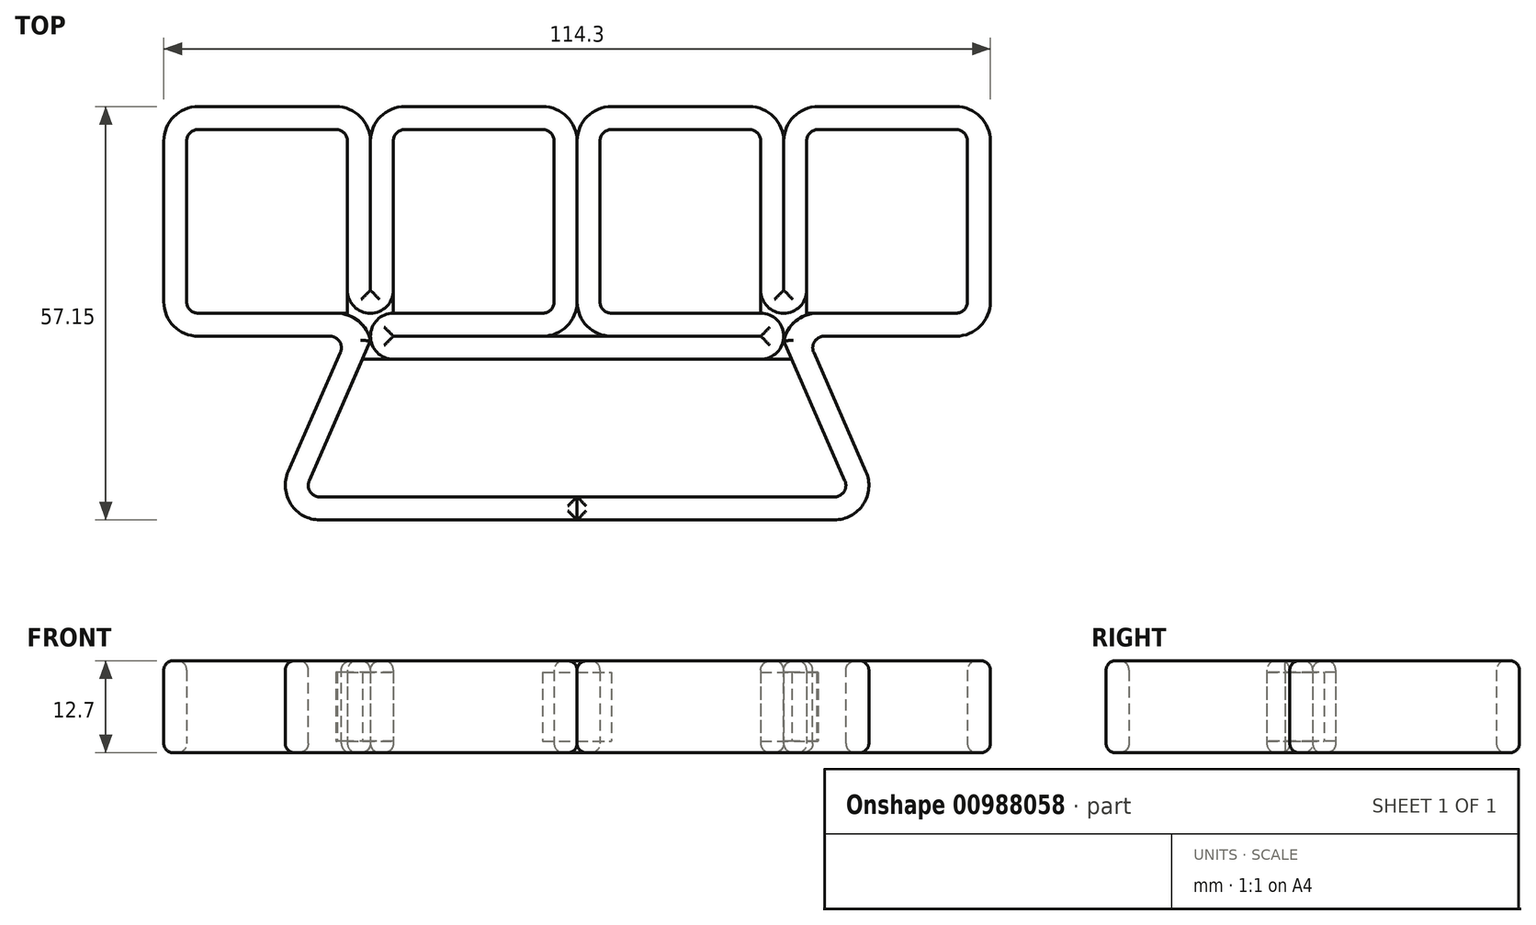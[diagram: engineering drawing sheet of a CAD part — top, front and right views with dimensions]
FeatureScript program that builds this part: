
annotation { "Feature Type Name" : "Feature", "Feature Type Description" : "" }
export const myFeature = defineFeature(function(context is Context, id is Id, definition is map)
    precondition{}
    {
        {
            var Q0;
            Q0=qCreatedBy(makeId("Top.planeOp"),FACE);
            var sketch = newSketch(context, id + "F0", { "sketchPlane" : qUnion([Q0])});
            skLineSegment(sketch, "E0.bottom", {"start": v(3.18, 3.17) * mm, "end": v(25.4, 3.18) * mm});
            skLineSegment(sketch, "E0.top", {"start": v(3.17, 28.58) * mm, "end": v(25.4, 28.58) * mm});
            skLineSegment(sketch, "E0.left", {"start": v(3.18, 3.18) * mm, "end": v(3.17, 28.57) * mm});
            skLineSegment(sketch, "E0.right", {"start": v(25.4, 3.18) * mm, "end": v(25.4, 28.58) * mm});
            skLineSegment(sketch, "E1.bottom", {"start": v(-3.17, 3.17) * mm, "end": v(-25.4, 3.17) * mm});
            skLineSegment(sketch, "E1.top", {"start": v(-3.18, 28.58) * mm, "end": v(-25.4, 28.57) * mm});
            skLineSegment(sketch, "E1.left", {"start": v(-3.17, 3.18) * mm, "end": v(-3.18, 28.57) * mm});
            skLineSegment(sketch, "E1.right", {"start": v(-25.4, 3.17) * mm, "end": v(-25.4, 28.57) * mm});
            skLineSegment(sketch, "E2", {"start": v(-25.4, 0) * mm, "end": v(25.4, 0) * mm});
            skLineSegment(sketch, "E3", {"start": v(-25.4, 3.17) * mm, "end": v(-28.58, 3.17) * mm});
            skLineSegment(sketch, "E4", {"start": v(-28.58, 3.18) * mm, "end": v(-28.58, -3.18) * mm});
            skLineSegment(sketch, "E5", {"start": v(-28.58, -3.18) * mm, "end": v(28.58, -3.17) * mm});
            skLineSegment(sketch, "E6", {"start": v(28.58, -3.18) * mm, "end": v(28.58, 3.18) * mm});
            skLineSegment(sketch, "E7", {"start": v(28.58, 3.18) * mm, "end": v(25.4, 3.18) * mm});
            skLineSegment(sketch, "E8", {"start": v(0, 0) * mm, "end": v(0, 31.75) * mm});
            skLineSegment(sketch, "E9", {"start": v(0, 31.75) * mm, "end": v(28.58, 31.75) * mm});
            skLineSegment(sketch, "E10", {"start": v(28.57, 31.75) * mm, "end": v(28.57, 6.35) * mm});
            skLineSegment(sketch, "E11", {"start": v(28.58, 31.75) * mm, "end": v(57.15, 31.75) * mm});
            skLineSegment(sketch, "E12", {"start": v(57.15, 31.75) * mm, "end": v(57.15, 0) * mm});
            skLineSegment(sketch, "E13.bottom", {"start": v(31.75, 3.18) * mm, "end": v(53.98, 3.18) * mm});
            skLineSegment(sketch, "E13.top", {"start": v(31.75, 28.58) * mm, "end": v(53.98, 28.58) * mm});
            skLineSegment(sketch, "E13.left", {"start": v(31.75, 3.18) * mm, "end": v(31.75, 28.58) * mm});
            skLineSegment(sketch, "E13.right", {"start": v(53.98, 3.18) * mm, "end": v(53.98, 28.58) * mm});
            skLineSegment(sketch, "E14", {"start": v(31.75, 3.18) * mm, "end": v(28.58, 3.18) * mm});
            skLineSegment(sketch, "E15", {"start": v(57.15, 0) * mm, "end": v(31.75, 0) * mm});
            skLineSegment(sketch, "E16", {"start": v(31.75, 0) * mm, "end": v(42.86, -25.4) * mm});
            skPoint(sketch, "E16.endSnap0", {"position": v(42.86, 3.18) * mm});
            skLineSegment(sketch, "E17", {"start": v(42.86, -25.4) * mm, "end": v(0, -25.4) * mm});
            skLineSegment(sketch, "E18", {"start": v(0, -22.23) * mm, "end": v(38, -22.22) * mm});
            skLineSegment(sketch, "E19", {"start": v(38, -22.23) * mm, "end": v(28.58, -0.66) * mm});
            skLineSegment(sketch, "E20.MirrorCS", {"start": v(0, 31.75) * mm, "end": v(-28.58, 31.75) * mm});
            skLineSegment(sketch, "E21.MirrorCS", {"start": v(-31.75, 3.18) * mm, "end": v(-31.75, 28.58) * mm});
            skLineSegment(sketch, "E22.MirrorCS", {"start": v(-28.58, 31.75) * mm, "end": v(-28.58, 6.35) * mm});
            skLineSegment(sketch, "E23.MirrorCS", {"start": v(-28.58, 31.75) * mm, "end": v(-57.15, 31.75) * mm});
            skLineSegment(sketch, "E24.MirrorCS", {"start": v(-31.75, 28.58) * mm, "end": v(-53.98, 28.58) * mm});
            skLineSegment(sketch, "E25.MirrorCS", {"start": v(-31.75, 3.18) * mm, "end": v(-53.98, 3.18) * mm});
            skLineSegment(sketch, "E26.MirrorCS", {"start": v(-57.15, 31.75) * mm, "end": v(-57.15, 0) * mm});
            skLineSegment(sketch, "E27.MirrorCS", {"start": v(-53.98, 3.18) * mm, "end": v(-53.98, 28.58) * mm});
            skLineSegment(sketch, "E28.MirrorCS", {"start": v(-57.15, 0) * mm, "end": v(-31.75, 0) * mm});
            skLineSegment(sketch, "E29.MirrorCS", {"start": v(-31.75, 0) * mm, "end": v(-42.86, -25.4) * mm});
            skLineSegment(sketch, "E30.MirrorCS", {"start": v(-38, -22.23) * mm, "end": v(-28.58, -0.66) * mm});
            skLineSegment(sketch, "E31.MirrorCS", {"start": v(0, -22.23) * mm, "end": v(-38, -22.23) * mm});
            skLineSegment(sketch, "E32.MirrorCS", {"start": v(-42.86, -25.4) * mm, "end": v(0, -25.4) * mm});
            skLineSegment(sketch, "E33", {"start": v(-31.75, 3.17) * mm, "end": v(-28.58, 3.17) * mm});
            skLineSegment(sketch, "E34", {"start": v(0, -22.23) * mm, "end": v(0, -25.4) * mm});
            skLineSegment(sketch, "E35.bottom", {"start": v(-28.57, 6.35) * mm, "end": v(-28.58, 6.35) * mm});
            skLineSegment(sketch, "E35.top", {"start": v(-28.57, 31.75) * mm, "end": v(-28.58, 31.75) * mm});
            skLineSegment(sketch, "E35.left", {"start": v(-28.57, 6.35) * mm, "end": v(-28.57, 31.75) * mm});
            skLineSegment(sketch, "E35.right", {"start": v(-28.58, 6.35) * mm, "end": v(-28.58, 31.75) * mm});
            skPoint(sketch, "E35.middle", {"position": v(-28.58, 19.05) * mm});
            skLineSegment(sketch, "E36.bottom", {"start": v(-31.75, 3.17) * mm, "end": v(-25.4, 3.17) * mm});
            skLineSegment(sketch, "E36.top", {"start": v(-31.75, 3.18) * mm, "end": v(-25.4, 3.18) * mm});
            skLineSegment(sketch, "E36.left", {"start": v(-31.75, 3.18) * mm, "end": v(-31.75, 3.18) * mm});
            skLineSegment(sketch, "E36.right", {"start": v(-25.4, 3.18) * mm, "end": v(-25.4, 3.18) * mm});
            skLineSegment(sketch, "E37.bottom", {"start": v(0, 0) * mm, "end": v(0, 0) * mm});
            skLineSegment(sketch, "E37.top", {"start": v(0, 31.75) * mm, "end": v(0, 31.75) * mm});
            skPoint(sketch, "E37.middle", {"position": v(0, 15.87) * mm});
            skLineSegment(sketch, "E38.left", {"start": v(-25.4, 0) * mm, "end": v(-25.4, 0) * mm});
            skLineSegment(sketch, "E38.right", {"start": v(25.4, 0) * mm, "end": v(25.4, 0) * mm});
            skLineSegment(sketch, "E39.bottom", {"start": v(28.58, 6.35) * mm, "end": v(28.57, 6.35) * mm});
            skLineSegment(sketch, "E39.top", {"start": v(28.58, 31.75) * mm, "end": v(28.57, 31.75) * mm});
            skLineSegment(sketch, "E39.left", {"start": v(28.58, 6.35) * mm, "end": v(28.58, 31.75) * mm});
            skLineSegment(sketch, "E39.right", {"start": v(28.57, 6.35) * mm, "end": v(28.57, 31.75) * mm});
            skPoint(sketch, "E39.middle", {"position": v(28.58, 19.05) * mm});
            skLineSegment(sketch, "E40.bottom", {"start": v(25.4, 3.18) * mm, "end": v(31.75, 3.18) * mm});
            skLineSegment(sketch, "E40.top", {"start": v(25.4, 3.18) * mm, "end": v(31.75, 3.18) * mm});
            skLineSegment(sketch, "E40.left", {"start": v(25.4, 3.18) * mm, "end": v(25.4, 3.18) * mm});
            skLineSegment(sketch, "E40.right", {"start": v(31.75, 3.18) * mm, "end": v(31.75, 3.18) * mm});
            skLineSegment(sketch, "E41.bottom", {"start": v(28.58, 3.18) * mm, "end": v(28.57, 3.18) * mm});
            skLineSegment(sketch, "E41.top", {"start": v(28.58, -3.17) * mm, "end": v(28.57, -3.17) * mm});
            skLineSegment(sketch, "E41.left", {"start": v(28.58, 3.18) * mm, "end": v(28.58, -3.18) * mm});
            skLineSegment(sketch, "E41.right", {"start": v(28.57, 3.18) * mm, "end": v(28.57, -3.17) * mm});
            skLineSegment(sketch, "E42.bottom", {"start": v(-28.58, 3.17) * mm, "end": v(-28.57, 3.17) * mm});
            skLineSegment(sketch, "E42.top", {"start": v(-28.58, -3.18) * mm, "end": v(-28.57, -3.18) * mm});
            skLineSegment(sketch, "E42.left", {"start": v(-28.58, 3.17) * mm, "end": v(-28.58, -3.17) * mm});
            skLineSegment(sketch, "E42.right", {"start": v(-28.57, 3.17) * mm, "end": v(-28.57, -3.18) * mm});
            skLineSegment(sketch, "E43.bottom", {"start": v(0, -25.4) * mm, "end": v(0, -25.4) * mm});
            skLineSegment(sketch, "E43.top", {"start": v(0, -22.23) * mm, "end": v(0, -22.23) * mm});
            skLineSegment(sketch, "E43.left", {"start": v(0, -25.4) * mm, "end": v(0, -22.23) * mm});
            skLineSegment(sketch, "E43.right", {"start": v(0, -25.4) * mm, "end": v(0, -22.23) * mm});
            skPoint(sketch, "E43.middle", {"position": v(0, -23.81) * mm});
            skSolve(sketch);
        }
        {
            var Q0;
            {var subQ38=sQuery(id+"F0.wireOp",EDGE,"E0.bottom");Q0=makeQuery(id+"F0.imprint","IMPRINT",FACE,{"disambiguationData":[TD([[makeQuery(id+"F0.imprint","IMPRINT",EDGE,{"derivedFrom":subQ38}),-1.0]])]});}
            extrude(context, id + "F1", {"entities" : qUnion([Q0]), "depth" : 6.35 * mm, "offsetDistance" : 25.4 * mm, "hasSecondDirection" : true, "secondDirectionOppositeDirection" : true, "secondDirectionDepth" : 6.35 * mm});
        }
        {
            var Q0;
            Q0=makeQuery(id+"F1.opExtrude","SWEPT_EDGE",EDGE,{"disambiguationData":[OSD([sQuery(id+"F0.wireOp",EDGE,"E24.MirrorCS"),sQuery(id+"F0.wireOp",EDGE,"E27.MirrorCS")])]});
            var Q1;
            Q1=makeQuery(id+"F1.opExtrude","SWEPT_EDGE",EDGE,{"disambiguationData":[OSD([sQuery(id+"F0.wireOp",EDGE,"E25.MirrorCS"),sQuery(id+"F0.wireOp",EDGE,"E27.MirrorCS")])]});
            var Q2;
            Q2=makeQuery(id+"F1.opExtrude","SWEPT_EDGE",EDGE,{"disambiguationData":[OSD([sQuery(id+"F0.wireOp",EDGE,"E21.MirrorCS"),sQuery(id+"F0.wireOp",EDGE,"E24.MirrorCS")])]});
            var Q3;
            Q3=makeQuery(id+"F1.opExtrude","SWEPT_EDGE",EDGE,{"disambiguationData":[OSD([sQuery(id+"F0.wireOp",EDGE,"E1.top"),sQuery(id+"F0.wireOp",EDGE,"E1.left")])]});
            var Q4;
            Q4=makeQuery(id+"F1.opExtrude","SWEPT_EDGE",EDGE,{"disambiguationData":[OSD([sQuery(id+"F0.wireOp",EDGE,"E1.top"),sQuery(id+"F0.wireOp",EDGE,"E1.right")])]});
            var Q5;
            Q5=makeQuery(id+"F1.opExtrude","SWEPT_EDGE",EDGE,{"disambiguationData":[OSD([sQuery(id+"F0.wireOp",EDGE,"E1.bottom"),sQuery(id+"F0.wireOp",EDGE,"E1.left")])]});
            var Q6;
            Q6=makeQuery(id+"F1.opExtrude","SWEPT_EDGE",EDGE,{"disambiguationData":[OSD([sQuery(id+"F0.wireOp",EDGE,"E0.top"),sQuery(id+"F0.wireOp",EDGE,"E0.left")])]});
            var Q7;
            Q7=makeQuery(id+"F1.opExtrude","SWEPT_EDGE",EDGE,{"disambiguationData":[OSD([sQuery(id+"F0.wireOp",EDGE,"E0.bottom"),sQuery(id+"F0.wireOp",EDGE,"E0.left")])]});
            var Q8;
            Q8=makeQuery(id+"F1.opExtrude","SWEPT_EDGE",EDGE,{"disambiguationData":[OSD([sQuery(id+"F0.wireOp",EDGE,"E0.top"),sQuery(id+"F0.wireOp",EDGE,"E0.right")])]});
            var Q9;
            Q9=makeQuery(id+"F1.opExtrude","SWEPT_EDGE",EDGE,{"disambiguationData":[OSD([sQuery(id+"F0.wireOp",EDGE,"E13.top"),sQuery(id+"F0.wireOp",EDGE,"E13.right")])]});
            var Q10;
            Q10=makeQuery(id+"F1.opExtrude","SWEPT_EDGE",EDGE,{"disambiguationData":[OSD([sQuery(id+"F0.wireOp",EDGE,"E13.bottom"),sQuery(id+"F0.wireOp",EDGE,"E13.right")])]});
            var Q11;
            Q11=makeQuery(id+"F1.opExtrude","SWEPT_EDGE",EDGE,{"disambiguationData":[OSD([sQuery(id+"F0.wireOp",EDGE,"E13.top"),sQuery(id+"F0.wireOp",EDGE,"E13.left")])]});
            var Q12;
            Q12=makeQuery(id+"F1.opExtrude","SWEPT_EDGE",EDGE,{"disambiguationData":[OSD([sQuery(id+"F0.wireOp",EDGE,"E18"),sQuery(id+"F0.wireOp",EDGE,"E19")])]});
            var Q13;
            Q13=makeQuery(id+"F1.opExtrude","SWEPT_EDGE",EDGE,{"disambiguationData":[OSD([sQuery(id+"F0.wireOp",EDGE,"E30.MirrorCS"),sQuery(id+"F0.wireOp",EDGE,"E31.MirrorCS")])]});
            var Q14;
            Q14=makeQuery(id+"F1.opExtrude","SWEPT_EDGE",EDGE,{"disambiguationData":[OSD([sQuery(id+"F0.wireOp",EDGE,"E28.MirrorCS"),sQuery(id+"F0.wireOp",EDGE,"E29.MirrorCS")])]});
            var Q15;
            Q15=makeQuery(id+"F1.opExtrude","SWEPT_EDGE",EDGE,{"disambiguationData":[OSD([sQuery(id+"F0.wireOp",EDGE,"E15"),sQuery(id+"F0.wireOp",EDGE,"E16")])]});
            fillet(context, id + "F2", {"entities" : qUnion([Q0, Q1, Q2, Q3, Q4, Q5, Q6, Q7, Q8, Q9, Q10, Q11, Q12, Q13, Q14, Q15]), "radius" : 1.59 * mm, "tangentPropagation" : true, "allowEdgeOverflow" : false});
        }
        {
            var Q0;
            Q0=makeQuery(id+"F1.opExtrude","SWEPT_EDGE",EDGE,{"disambiguationData":[OSD([sQuery(id+"F0.wireOp",EDGE,"E26.MirrorCS"),sQuery(id+"F0.wireOp",EDGE,"E28.MirrorCS")])]});
            var Q1;
            Q1=makeQuery(id+"F1.opExtrude","SWEPT_EDGE",EDGE,{"disambiguationData":[OSD([sQuery(id+"F0.wireOp",EDGE,"E23.MirrorCS"),sQuery(id+"F0.wireOp",EDGE,"E26.MirrorCS")])]});
            var Q2;
            Q2=makeQuery(id+"F1.opExtrude","SWEPT_EDGE",EDGE,{"disambiguationData":[OSD([sQuery(id+"F0.wireOp",EDGE,"E29.MirrorCS"),sQuery(id+"F0.wireOp",EDGE,"E32.MirrorCS")])]});
            var Q3;
            Q3=makeQuery(id+"F1.opExtrude","SWEPT_EDGE",EDGE,{"disambiguationData":[OSD([sQuery(id+"F0.wireOp",EDGE,"E3"),sQuery(id+"F0.wireOp",EDGE,"E4"),sQuery(id+"F0.wireOp",EDGE,"E33")])]});
            var Q4;
            Q4=makeQuery(id+"F1.opExtrude","SWEPT_EDGE",EDGE,{"disambiguationData":[OSD([sQuery(id+"F0.wireOp",EDGE,"E6"),sQuery(id+"F0.wireOp",EDGE,"E7"),sQuery(id+"F0.wireOp",EDGE,"E14")])]});
            var Q5;
            Q5=makeQuery(id+"F1.opExtrude","SWEPT_EDGE",EDGE,{"disambiguationData":[OSD([sQuery(id+"F0.wireOp",EDGE,"E16"),sQuery(id+"F0.wireOp",EDGE,"E17")])]});
            var Q6;
            Q6=makeQuery(id+"F1.opExtrude","SWEPT_EDGE",EDGE,{"disambiguationData":[OSD([sQuery(id+"F0.wireOp",EDGE,"E12"),sQuery(id+"F0.wireOp",EDGE,"E15")])]});
            var Q7;
            Q7=makeQuery(id+"F1.opExtrude","SWEPT_EDGE",EDGE,{"disambiguationData":[OSD([sQuery(id+"F0.wireOp",EDGE,"E11"),sQuery(id+"F0.wireOp",EDGE,"E12")])]});
            var Q8;
            Q8=makeQuery(id+"F1.opExtrude","SWEPT_EDGE",EDGE,{"disambiguationData":[OSD([sQuery(id+"F0.wireOp",EDGE,"E11"),sQuery(id+"F0.wireOp",EDGE,"E39.left")])]});
            var Q9;
            Q9=makeQuery(id+"F1.opExtrude","SWEPT_EDGE",EDGE,{"disambiguationData":[OSD([sQuery(id+"F0.wireOp",EDGE,"E9"),sQuery(id+"F0.wireOp",EDGE,"E39.right")])]});
            var Q10;
            Q10=makeQuery(id+"F1.opExtrude","SWEPT_EDGE",EDGE,{"disambiguationData":[OSD([sQuery(id+"F0.wireOp",EDGE,"E20.MirrorCS"),sQuery(id+"F0.wireOp",EDGE,"E35.left")])]});
            var Q11;
            Q11=makeQuery(id+"F1.opExtrude","SWEPT_EDGE",EDGE,{"disambiguationData":[OSD([sQuery(id+"F0.wireOp",EDGE,"E23.MirrorCS"),sQuery(id+"F0.wireOp",EDGE,"E35.right")])]});
            var Q12;
            Q12=makeQuery(id+"F1.opExtrude","SWEPT_EDGE",EDGE,{"disambiguationData":[OSD([sQuery(id+"F0.wireOp",EDGE,"E9"),sQuery(id+"F0.wireOp",EDGE,"E8")])]});
            var Q13;
            Q13=makeQuery(id+"F1.opExtrude","SWEPT_EDGE",EDGE,{"disambiguationData":[OSD([sQuery(id+"F0.wireOp",EDGE,"E20.MirrorCS"),sQuery(id+"F0.wireOp",EDGE,"E8")])]});
            var Q14;
            Q14=makeQuery(id+"F1.opExtrude","SWEPT_EDGE",EDGE,{"disambiguationData":[OSD([sQuery(id+"F0.wireOp",EDGE,"E8"),sQuery(id+"F0.wireOp",EDGE,"E2")])]});
            var Q15;
            Q15=makeQuery(id+"F1.opExtrude","SWEPT_EDGE",EDGE,{"disambiguationData":[OSD([sQuery(id+"F0.wireOp",EDGE,"E8"),sQuery(id+"F0.wireOp",EDGE,"E2")])]});
            fillet(context, id + "F3", {"entities" : qUnion([Q0, Q1, Q2, Q3, Q4, Q5, Q6, Q7, Q8, Q9, Q10, Q11, Q12, Q13, Q14, Q15]), "radius" : 4.76 * mm, "tangentPropagation" : true, "allowEdgeOverflow" : false});
        }
        {
            var Q0;
            Q0=makeQuery(id+"F1.opExtrude","SWEPT_EDGE",EDGE,{"disambiguationData":[OSD([sQuery(id+"F0.wireOp",EDGE,"E21.MirrorCS"),sQuery(id+"F0.wireOp",EDGE,"E36.top")])]});
            var Q1;
            Q1=makeQuery(id+"F1.opExtrude","SWEPT_EDGE",EDGE,{"disambiguationData":[OSD([sQuery(id+"F0.wireOp",EDGE,"E1.right"),sQuery(id+"F0.wireOp",EDGE,"E36.top")])]});
            var Q2;
            Q2=makeQuery(id+"F1.opExtrude","SWEPT_EDGE",EDGE,{"disambiguationData":[OSD([sQuery(id+"F0.wireOp",EDGE,"E13.left"),sQuery(id+"F0.wireOp",EDGE,"E40.top")])]});
            var Q3;
            Q3=makeQuery(id+"F1.opExtrude","SWEPT_EDGE",EDGE,{"disambiguationData":[OSD([sQuery(id+"F0.wireOp",EDGE,"E0.right"),sQuery(id+"F0.wireOp",EDGE,"E40.top")])]});
            var Q4;
            Q4=makeQuery(id+"F1.opExtrude","SWEPT_EDGE",EDGE,{"disambiguationData":[OSD([sQuery(id+"F0.wireOp",EDGE,"E5"),sQuery(id+"F0.wireOp",EDGE,"E41.right")])]});
            var Q5;
            Q5=makeQuery(id+"F1.opExtrude","SWEPT_EDGE",EDGE,{"disambiguationData":[OSD([sQuery(id+"F0.wireOp",EDGE,"E7"),sQuery(id+"F0.wireOp",EDGE,"E41.right")])]});
            var Q6;
            Q6=makeQuery(id+"F1.opExtrude","SWEPT_EDGE",EDGE,{"disambiguationData":[OSD([sQuery(id+"F0.wireOp",EDGE,"E3"),sQuery(id+"F0.wireOp",EDGE,"E42.right")])]});
            var Q7;
            Q7=makeQuery(id+"F1.opExtrude","SWEPT_EDGE",EDGE,{"disambiguationData":[OSD([sQuery(id+"F0.wireOp",EDGE,"E5"),sQuery(id+"F0.wireOp",EDGE,"E42.right")])]});
            fillet(context, id + "F4", {"entities" : qUnion([Q0, Q1, Q2, Q3, Q4, Q5, Q6, Q7]), "radius" : 3.17 * mm, "tangentPropagation" : true, "allowEdgeOverflow" : false});
        }
        {
            var Q0;
            Q0=makeQuery(id+"F1.opExtrude","CAP_FACE",FACE,{"disambiguationData":[OSD([sQuery(id+"F0.wireOp",EDGE,"E0.bottom"),sQuery(id+"F0.wireOp",EDGE,"E0.top"),sQuery(id+"F0.wireOp",EDGE,"E0.left"),sQuery(id+"F0.wireOp",EDGE,"E0.right"),sQuery(id+"F0.wireOp",EDGE,"E1.bottom"),sQuery(id+"F0.wireOp",EDGE,"E1.top"),sQuery(id+"F0.wireOp",EDGE,"E1.left"),sQuery(id+"F0.wireOp",EDGE,"E1.right"),sQuery(id+"F0.wireOp",EDGE,"E2"),sQuery(id+"F0.wireOp",EDGE,"E3"),sQuery(id+"F0.wireOp",EDGE,"E4"),sQuery(id+"F0.wireOp",EDGE,"E5"),sQuery(id+"F0.wireOp",EDGE,"E6"),sQuery(id+"F0.wireOp",EDGE,"E7"),sQuery(id+"F0.wireOp",EDGE,"E9"),sQuery(id+"F0.wireOp",EDGE,"E11"),sQuery(id+"F0.wireOp",EDGE,"E12"),sQuery(id+"F0.wireOp",EDGE,"E13.bottom"),sQuery(id+"F0.wireOp",EDGE,"E13.top"),sQuery(id+"F0.wireOp",EDGE,"E13.left"),sQuery(id+"F0.wireOp",EDGE,"E13.right"),sQuery(id+"F0.wireOp",EDGE,"E14"),sQuery(id+"F0.wireOp",EDGE,"E15"),sQuery(id+"F0.wireOp",EDGE,"E16"),sQuery(id+"F0.wireOp",EDGE,"E17"),sQuery(id+"F0.wireOp",EDGE,"E18"),sQuery(id+"F0.wireOp",EDGE,"E19"),sQuery(id+"F0.wireOp",EDGE,"E20.MirrorCS"),sQuery(id+"F0.wireOp",EDGE,"E21.MirrorCS"),sQuery(id+"F0.wireOp",EDGE,"E23.MirrorCS"),sQuery(id+"F0.wireOp",EDGE,"E24.MirrorCS"),sQuery(id+"F0.wireOp",EDGE,"E25.MirrorCS"),sQuery(id+"F0.wireOp",EDGE,"E26.MirrorCS"),sQuery(id+"F0.wireOp",EDGE,"E27.MirrorCS"),sQuery(id+"F0.wireOp",EDGE,"E28.MirrorCS"),sQuery(id+"F0.wireOp",EDGE,"E29.MirrorCS"),sQuery(id+"F0.wireOp",EDGE,"E30.MirrorCS"),sQuery(id+"F0.wireOp",EDGE,"E31.MirrorCS"),sQuery(id+"F0.wireOp",EDGE,"E32.MirrorCS"),sQuery(id+"F0.wireOp",EDGE,"E33"),sQuery(id+"F0.wireOp",EDGE,"E35.bottom"),sQuery(id+"F0.wireOp",EDGE,"E35.left"),sQuery(id+"F0.wireOp",EDGE,"E35.right"),sQuery(id+"F0.wireOp",EDGE,"E36.top"),sQuery(id+"F0.wireOp",EDGE,"E8"),sQuery(id+"F0.wireOp",EDGE,"E8"),sQuery(id+"F0.wireOp",EDGE,"E2"),sQuery(id+"F0.wireOp",EDGE,"E38.left"),sQuery(id+"F0.wireOp",EDGE,"E38.right"),sQuery(id+"F0.wireOp",EDGE,"E39.bottom"),sQuery(id+"F0.wireOp",EDGE,"E39.left"),sQuery(id+"F0.wireOp",EDGE,"E39.right"),sQuery(id+"F0.wireOp",EDGE,"E40.top"),sQuery(id+"F0.wireOp",EDGE,"E41.right"),sQuery(id+"F0.wireOp",EDGE,"E42.right"),sQuery(id+"F0.wireOp",EDGE,"E43.left"),sQuery(id+"F0.wireOp",EDGE,"E43.right")])],"isStart":true});
            var Q1;
            Q1=makeQuery(id+"F1.opExtrude","CAP_FACE",FACE,{"disambiguationData":[OSD([sQuery(id+"F0.wireOp",EDGE,"E0.bottom"),sQuery(id+"F0.wireOp",EDGE,"E0.top"),sQuery(id+"F0.wireOp",EDGE,"E0.left"),sQuery(id+"F0.wireOp",EDGE,"E0.right"),sQuery(id+"F0.wireOp",EDGE,"E1.bottom"),sQuery(id+"F0.wireOp",EDGE,"E1.top"),sQuery(id+"F0.wireOp",EDGE,"E1.left"),sQuery(id+"F0.wireOp",EDGE,"E1.right"),sQuery(id+"F0.wireOp",EDGE,"E2"),sQuery(id+"F0.wireOp",EDGE,"E3"),sQuery(id+"F0.wireOp",EDGE,"E4"),sQuery(id+"F0.wireOp",EDGE,"E5"),sQuery(id+"F0.wireOp",EDGE,"E6"),sQuery(id+"F0.wireOp",EDGE,"E7"),sQuery(id+"F0.wireOp",EDGE,"E9"),sQuery(id+"F0.wireOp",EDGE,"E11"),sQuery(id+"F0.wireOp",EDGE,"E12"),sQuery(id+"F0.wireOp",EDGE,"E13.bottom"),sQuery(id+"F0.wireOp",EDGE,"E13.top"),sQuery(id+"F0.wireOp",EDGE,"E13.left"),sQuery(id+"F0.wireOp",EDGE,"E13.right"),sQuery(id+"F0.wireOp",EDGE,"E14"),sQuery(id+"F0.wireOp",EDGE,"E15"),sQuery(id+"F0.wireOp",EDGE,"E16"),sQuery(id+"F0.wireOp",EDGE,"E17"),sQuery(id+"F0.wireOp",EDGE,"E18"),sQuery(id+"F0.wireOp",EDGE,"E19"),sQuery(id+"F0.wireOp",EDGE,"E20.MirrorCS"),sQuery(id+"F0.wireOp",EDGE,"E21.MirrorCS"),sQuery(id+"F0.wireOp",EDGE,"E23.MirrorCS"),sQuery(id+"F0.wireOp",EDGE,"E24.MirrorCS"),sQuery(id+"F0.wireOp",EDGE,"E25.MirrorCS"),sQuery(id+"F0.wireOp",EDGE,"E26.MirrorCS"),sQuery(id+"F0.wireOp",EDGE,"E27.MirrorCS"),sQuery(id+"F0.wireOp",EDGE,"E28.MirrorCS"),sQuery(id+"F0.wireOp",EDGE,"E29.MirrorCS"),sQuery(id+"F0.wireOp",EDGE,"E30.MirrorCS"),sQuery(id+"F0.wireOp",EDGE,"E31.MirrorCS"),sQuery(id+"F0.wireOp",EDGE,"E32.MirrorCS"),sQuery(id+"F0.wireOp",EDGE,"E33"),sQuery(id+"F0.wireOp",EDGE,"E35.bottom"),sQuery(id+"F0.wireOp",EDGE,"E35.left"),sQuery(id+"F0.wireOp",EDGE,"E35.right"),sQuery(id+"F0.wireOp",EDGE,"E36.top"),sQuery(id+"F0.wireOp",EDGE,"E8"),sQuery(id+"F0.wireOp",EDGE,"E8"),sQuery(id+"F0.wireOp",EDGE,"E2"),sQuery(id+"F0.wireOp",EDGE,"E38.left"),sQuery(id+"F0.wireOp",EDGE,"E38.right"),sQuery(id+"F0.wireOp",EDGE,"E39.bottom"),sQuery(id+"F0.wireOp",EDGE,"E39.left"),sQuery(id+"F0.wireOp",EDGE,"E39.right"),sQuery(id+"F0.wireOp",EDGE,"E40.top"),sQuery(id+"F0.wireOp",EDGE,"E41.right"),sQuery(id+"F0.wireOp",EDGE,"E42.right"),sQuery(id+"F0.wireOp",EDGE,"E43.left"),sQuery(id+"F0.wireOp",EDGE,"E43.right")])],"isStart":false});
            fillet(context, id + "F5", {"entities" : qUnion([Q0, Q1]), "radius" : 1.27 * mm, "tangentPropagation" : true, "allowEdgeOverflow" : false});
        }
        {
            var Q0;
            Q0=qCreatedBy(makeId("Top.planeOp"),FACE);
            var sketch = newSketch(context, id + "F6", { "sketchPlane" : qUnion([Q0])});
            skArc(sketch, "E44", {"start": v(28.57, 0) * mm, "mid": v(27.64, 2.25) * mm, "end": v(25.4, 3.18) * mm});
            skArc(sketch, "E45", {"start": v(25.4, -3.18) * mm, "mid": v(27.64, -2.25) * mm, "end": v(28.57, 0) * mm});
            skLineSegment(sketch, "E46", {"start": v(25.4, -3.18) * mm, "end": v(29.67, -3.18) * mm});
            skLineSegment(sketch, "E47", {"start": v(29.67, -3.17) * mm, "end": v(28.58, -0.66) * mm});
            skLineSegment(sketch, "E48", {"start": v(25.4, 3.18) * mm, "end": v(25.4, 6.35) * mm});
            skLineSegment(sketch, "E49", {"start": v(31.75, 6.35) * mm, "end": v(31.75, 3.18) * mm});
            skLineSegment(sketch, "E50", {"start": v(31.75, 3.18) * mm, "end": v(33.34, 3.18) * mm});
            skArc(sketch, "E51", {"start": v(25.4, 6.35) * mm, "mid": v(28.58, 3.18) * mm, "end": v(31.75, 6.35) * mm});
            skPoint(sketch, "E52", {"position": v(28.58, 3.18) * mm});
            skArc(sketch, "E53", {"start": v(33.34, 3.18) * mm, "mid": v(30.26, 2.12) * mm, "end": v(28.58, -0.66) * mm});
            skLineSegment(sketch, "E54", {"start": v(0, -25.8) * mm, "end": v(0, 31.22) * mm, "construction": true});
            skLineSegment(sketch, "E55.MirrorCS", {"start": v(-25.4, -3.18) * mm, "end": v(-29.67, -3.18) * mm});
            skArc(sketch, "E56.MirrorCS", {"start": v(-25.4, -3.18) * mm, "mid": v(-27.64, -2.25) * mm, "end": v(-28.57, 0) * mm});
            skLineSegment(sketch, "E57.MirrorCS", {"start": v(-29.67, -3.17) * mm, "end": v(-28.58, -0.66) * mm});
            skArc(sketch, "E58.MirrorCS", {"start": v(-33.34, 3.18) * mm, "mid": v(-30.26, 2.12) * mm, "end": v(-28.58, -0.66) * mm});
            skArc(sketch, "E59.MirrorCS", {"start": v(-28.57, 0) * mm, "mid": v(-27.64, 2.25) * mm, "end": v(-25.4, 3.18) * mm});
            skLineSegment(sketch, "E60.MirrorCS", {"start": v(-25.4, 3.18) * mm, "end": v(-25.4, 6.35) * mm});
            skArc(sketch, "E61.MirrorCS", {"start": v(-25.4, 6.35) * mm, "mid": v(-28.58, 3.18) * mm, "end": v(-31.75, 6.35) * mm});
            skLineSegment(sketch, "E62.MirrorCS", {"start": v(-31.75, 6.35) * mm, "end": v(-31.75, 3.18) * mm});
            skLineSegment(sketch, "E63.MirrorCS", {"start": v(-31.75, 3.18) * mm, "end": v(-33.34, 3.18) * mm});
            skLineSegment(sketch, "E64", {"start": v(-4.76, 0) * mm, "end": v(4.76, 0) * mm});
            skArc(sketch, "E65", {"start": v(0, 4.76) * mm, "mid": v(1.4, 1.4) * mm, "end": v(4.76, 0) * mm});
            skArc(sketch, "E66", {"start": v(-4.76, 0) * mm, "mid": v(-1.4, 1.4) * mm, "end": v(0, 4.76) * mm});
            skSolve(sketch);
        }
        {
            var Q0;
            Q0 = qSketchRegion(id + "F6", true);
            extrude(context, id + "F7", {"entities" : qUnion([Q0]), "depth" : 4.76 * mm, "offsetDistance" : 25.4 * mm, "hasSecondDirection" : true, "secondDirectionOppositeDirection" : true, "secondDirectionDepth" : 4.76 * mm});
        }
    });
